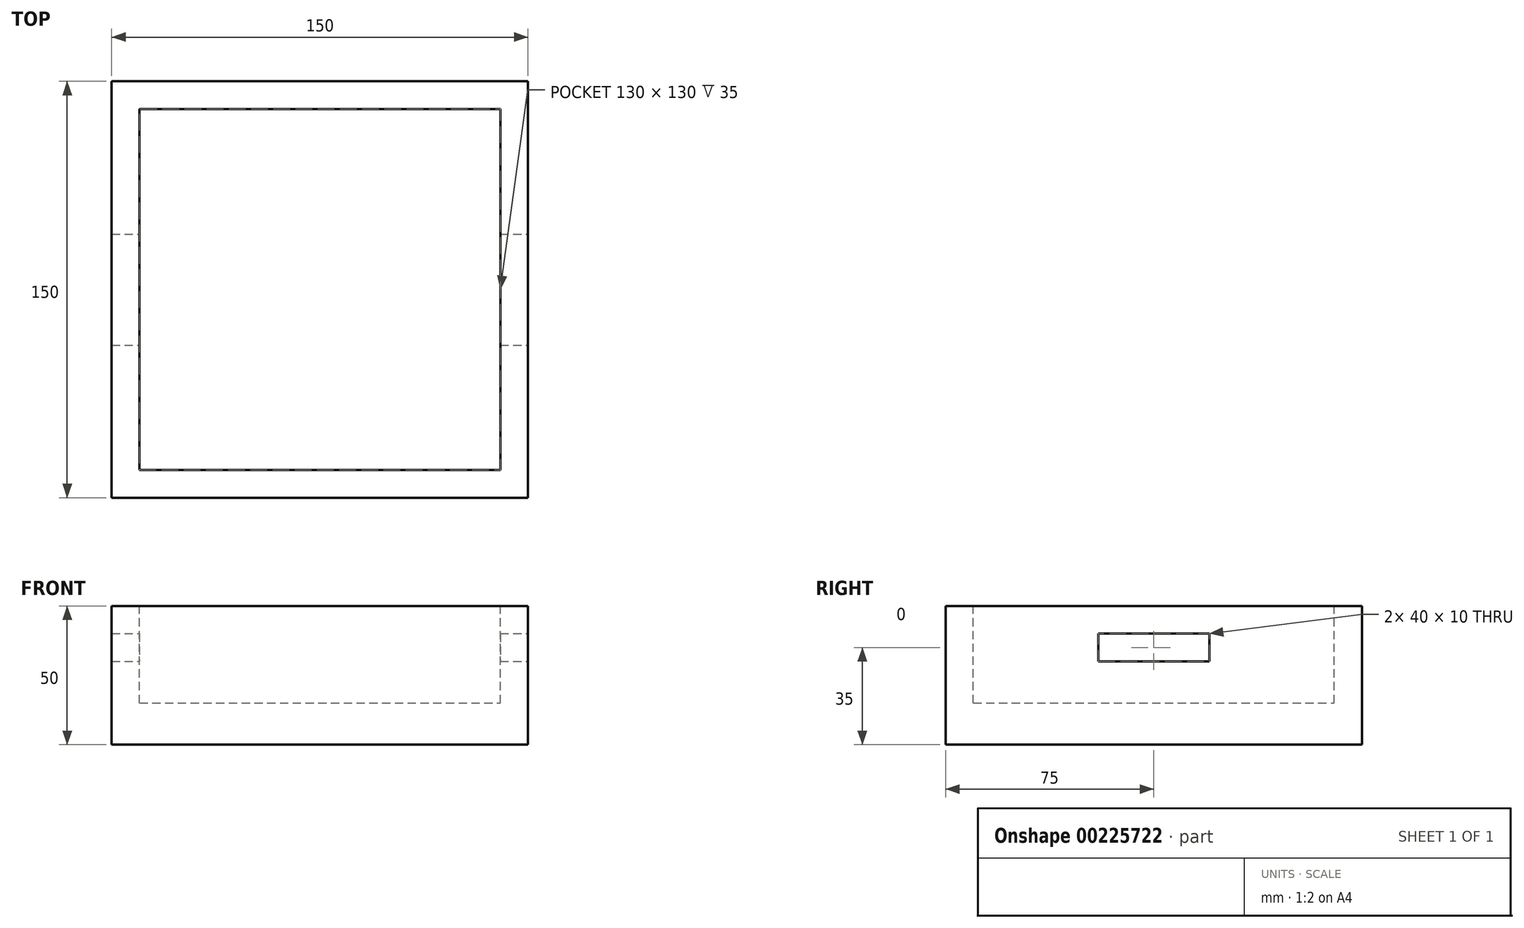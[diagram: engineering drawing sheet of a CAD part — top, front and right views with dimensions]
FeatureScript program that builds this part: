
annotation { "Feature Type Name" : "Feature", "Feature Type Description" : "" }
export const myFeature = defineFeature(function(context is Context, id is Id, definition is map)
    precondition{}
    {
        {
            var Q0;
            Q0=qCreatedBy(makeId("Top.planeOp"),FACE);
            var sketch = newSketch(context, id + "F0", { "sketchPlane" : qUnion([Q0])});
            skLineSegment(sketch, "E0.bottom", {"start": v(-75, 75) * mm, "end": v(75, 75) * mm});
            skLineSegment(sketch, "E0.top", {"start": v(-75, -75) * mm, "end": v(75, -75) * mm});
            skLineSegment(sketch, "E0.left", {"start": v(-75, 75) * mm, "end": v(-75, -75) * mm});
            skLineSegment(sketch, "E0.right", {"start": v(75, 75) * mm, "end": v(75, -75) * mm});
            skSolve(sketch);
        }
        {
            var Q0;
            Q0 = qSketchRegion(id + "F0", true);
            extrude(context, id + "F1", {"entities" : qUnion([Q0]), "depth" : 50 * mm});
        }
        {
            var Q0;
            Q0=makeQuery(id+"F1.opExtrude","CAP_FACE",FACE,{"disambiguationData":[OSD([sQuery(id+"F0.wireOp",EDGE,"E0.bottom"),sQuery(id+"F0.wireOp",EDGE,"E0.top"),sQuery(id+"F0.wireOp",EDGE,"E0.left"),sQuery(id+"F0.wireOp",EDGE,"E0.right")])],"isStart":false});
            var sketch = newSketch(context, id + "F2", { "sketchPlane" : qUnion([Q0])});
            skLineSegment(sketch, "E1.bottom", {"start": v(-65, -65) * mm, "end": v(65, -65) * mm});
            skLineSegment(sketch, "E1.top", {"start": v(-65, 65) * mm, "end": v(65, 65) * mm});
            skLineSegment(sketch, "E1.left", {"start": v(-65, -65) * mm, "end": v(-65, 65) * mm});
            skLineSegment(sketch, "E1.right", {"start": v(65, -65) * mm, "end": v(65, 65) * mm});
            skSolve(sketch);
        }
        {
            var Q0;
            Q0 = qSketchRegion(id + "F2", true);
            extrude(context, id + "F3", {"entities" : qUnion([Q0]), "operationType" : NewBodyOperationType.REMOVE, "oppositeDirection" : true, "depth" : 35 * mm});
        }
        {
            var Q0;
            Q0=makeQuery(id+"F1.opExtrude","SWEPT_FACE",FACE,{"disambiguationData":[OSD([sQuery(id+"F0.wireOp",EDGE,"E0.right")])]});
            var sketch = newSketch(context, id + "F4", { "sketchPlane" : qUnion([Q0])});
            skLineSegment(sketch, "E2.bottom", {"start": v(-20, 40) * mm, "end": v(20, 40) * mm});
            skLineSegment(sketch, "E2.top", {"start": v(-20, 30) * mm, "end": v(20, 30) * mm});
            skLineSegment(sketch, "E2.left", {"start": v(-20, 40) * mm, "end": v(-20, 30) * mm});
            skLineSegment(sketch, "E2.right", {"start": v(20, 40) * mm, "end": v(20, 30) * mm});
            skSolve(sketch);
        }
        {
            var Q0;
            Q0 = qSketchRegion(id + "F4", true);
            extrude(context, id + "F5", {"entities" : qUnion([Q0]), "operationType" : NewBodyOperationType.REMOVE, "endBound" : BoundingType.THROUGH_ALL, "oppositeDirection" : true, "depth" : 25 * mm});
        }
    });
